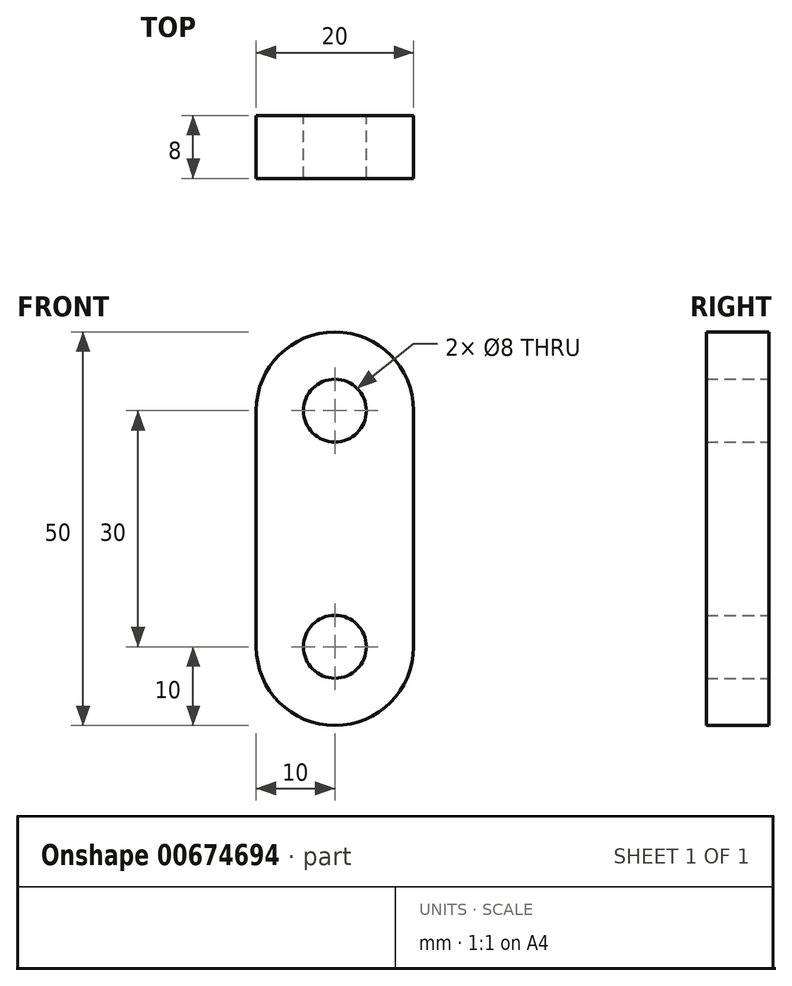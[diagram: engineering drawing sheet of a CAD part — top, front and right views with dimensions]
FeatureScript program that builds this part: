
annotation { "Feature Type Name" : "Feature", "Feature Type Description" : "" }
export const myFeature = defineFeature(function(context is Context, id is Id, definition is map)
    precondition{}
    {
        {
            var Q0;
            Q0=qCreatedBy(makeId("Front.planeOp"),FACE);
            var sketch = newSketch(context, id + "F0", { "sketchPlane" : qUnion([Q0])});
            skArc(sketch, "E0", {"start": v(-10, 0) * mm, "mid": v(0, -10) * mm, "end": v(10, 0) * mm});
            skArc(sketch, "E1", {"start": v(10, 30) * mm, "mid": v(0, 40) * mm, "end": v(-10, 30) * mm});
            skLineSegment(sketch, "E2", {"start": v(-10, 30) * mm, "end": v(-10, 0) * mm});
            skLineSegment(sketch, "E3", {"start": v(10, 30) * mm, "end": v(10, 0) * mm});
            skCircle(sketch, "E4", {"center": v(0, 30) * mm, "radius": 4 * mm});
            skCircle(sketch, "E5", {"center": v(0, 0) * mm, "radius": 4 * mm});
            skSolve(sketch);
        }
        {
            var Q0;
            Q0 = qSketchRegion(id + "F0", true);
            extrude(context, id + "F1", {"entities" : qUnion([Q0]), "depth" : 8 * mm, "offsetDistance" : 25 * mm});
        }
    });
